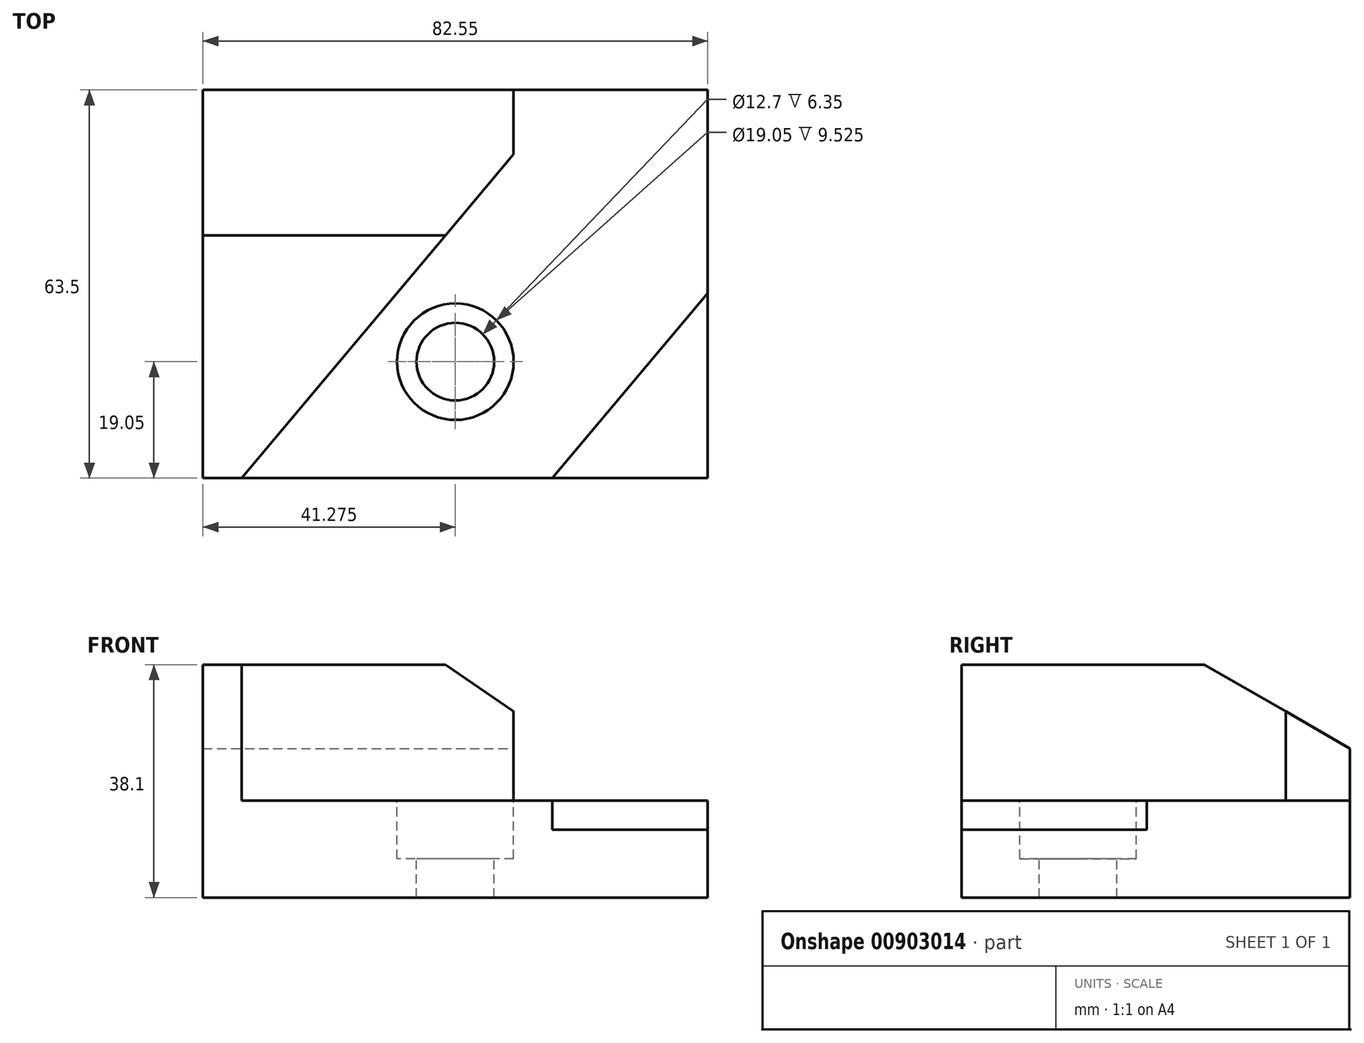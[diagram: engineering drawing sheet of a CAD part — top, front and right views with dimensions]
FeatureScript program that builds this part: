
annotation { "Feature Type Name" : "Feature", "Feature Type Description" : "" }
export const myFeature = defineFeature(function(context is Context, id is Id, definition is map)
    precondition{}
    {
        {
            var Q0;
            Q0=qCreatedBy(makeId("Front.planeOp"),FACE);
            var sketch = newSketch(context, id + "F0", { "sketchPlane" : qUnion([Q0])});
            skLineSegment(sketch, "E0.bottom", {"start": v(0, 0) * mm, "end": v(6.35, 0) * mm});
            skLineSegment(sketch, "E0.top", {"start": v(0, 38.1) * mm, "end": v(6.35, 38.1) * mm});
            skLineSegment(sketch, "E0.left", {"start": v(0, 0) * mm, "end": v(0, 38.1) * mm});
            skLineSegment(sketch, "E0.right", {"start": v(6.35, 0) * mm, "end": v(6.35, 38.1) * mm});
            skLineSegment(sketch, "E1", {"start": v(0, 0) * mm, "end": v(82.55, 0) * mm});
            skLineSegment(sketch, "E2", {"start": v(82.55, 0) * mm, "end": v(82.55, 11.11) * mm});
            skLineSegment(sketch, "E3", {"start": v(82.55, 11.11) * mm, "end": v(57.15, 11.11) * mm});
            skLineSegment(sketch, "E4", {"start": v(57.15, 11.11) * mm, "end": v(57.15, 15.87) * mm});
            skLineSegment(sketch, "E5", {"start": v(57.15, 15.87) * mm, "end": v(6.35, 15.87) * mm});
            skLineSegment(sketch, "E6", {"start": v(0, -8.47) * mm, "end": v(31.75, -8.47) * mm});
            skLineSegment(sketch, "E7.bottom", {"start": v(31.75, 0) * mm, "end": v(57.32, 0) * mm});
            skLineSegment(sketch, "E7.top", {"start": v(31.75, -4.76) * mm, "end": v(57.32, -4.76) * mm});
            skLineSegment(sketch, "E7.left", {"start": v(31.75, 0) * mm, "end": v(31.75, -4.76) * mm});
            skLineSegment(sketch, "E7.right", {"start": v(57.32, 0) * mm, "end": v(57.32, -4.76) * mm});
            skSolve(sketch);
        }
        {
            var Q0;
            {var subQ0=sQuery(id+"F0.wireOp",EDGE,"E2");Q0=makeQuery(id+"F0.imprint","IMPRINT",FACE,{"disambiguationData":[TD([[makeQuery(id+"F0.imprint","IMPRINT",EDGE,{"derivedFrom":subQ0}),1.0]])]});}
            var Q1;
            {var subQ1=sQuery(id+"F0.wireOp",EDGE,"E0.top");Q1=makeQuery(id+"F0.imprint","IMPRINT",FACE,{"disambiguationData":[TD([[makeQuery(id+"F0.imprint","IMPRINT",EDGE,{"derivedFrom":subQ1}),-1.0]])]});}
            var Q2;
            Q2=makeQuery(id+"F0.imprint","IMPRINT",FACE,{"disambiguationData":[TD([[makeQuery(id+"F0.imprint","IMPRINT",EDGE,{"derivedFrom":sQuery(id+"F0.wireOp",EDGE,"E7.bottom")}),-1.0]])]});
            extrude(context, id + "F1", {"entities" : qUnion([Q0, Q1, Q2]), "depth" : 63.5 * mm, "offsetDistance" : 25.4 * mm});
        }
        {
            var Q0;
            Q0=qCreatedBy(makeId("Top.planeOp"),FACE);
            var sketch = newSketch(context, id + "F2", { "sketchPlane" : qUnion([Q0])});
            skLineSegment(sketch, "E8", {"start": v(0, 10.1) * mm, "end": v(82.55, 10.1) * mm});
            skLineSegment(sketch, "E9", {"start": v(82.55, 0) * mm, "end": v(50.8, 0) * mm});
            skLineSegment(sketch, "E10", {"start": v(94.56, 0) * mm, "end": v(94.56, -63.5) * mm});
            skLineSegment(sketch, "E11", {"start": v(82.55, -63.5) * mm, "end": v(57.15, -63.5) * mm});
            skLineSegment(sketch, "E12", {"start": v(57.15, -63.5) * mm, "end": v(82.55, -33.23) * mm});
            skLineSegment(sketch, "E13", {"start": v(82.55, 0) * mm, "end": v(82.55, -63.5) * mm});
            skLineSegment(sketch, "E14", {"start": v(82.55, -33.23) * mm, "end": v(82.55, -63.5) * mm});
            skLineSegment(sketch, "E15", {"start": v(0, -76.09) * mm, "end": v(31.75, -76.09) * mm});
            skLineSegment(sketch, "E16", {"start": v(31.75, -76.09) * mm, "end": v(41.27, -76.09) * mm});
            skLineSegment(sketch, "E17", {"start": v(41.27, -63.5) * mm, "end": v(41.27, -44.45) * mm});
            skLineSegment(sketch, "E18", {"start": v(57.15, -63.5) * mm, "end": v(6.35, -63.5) * mm});
            skLineSegment(sketch, "E19", {"start": v(6.35, -63.5) * mm, "end": v(0, -63.5) * mm});
            skLineSegment(sketch, "E20", {"start": v(0, 0) * mm, "end": v(0, -23.81) * mm});
            skLineSegment(sketch, "E21", {"start": v(0, -23.81) * mm, "end": v(0, -63.5) * mm});
            skLineSegment(sketch, "E22", {"start": v(0, 0) * mm, "end": v(50.8, 0) * mm});
            skLineSegment(sketch, "E23", {"start": v(6.35, -63.5) * mm, "end": v(6.35, 0) * mm});
            skLineSegment(sketch, "E24", {"start": v(6.35, -63.5) * mm, "end": v(39.65, -23.81) * mm});
            skLineSegment(sketch, "E25", {"start": v(0, -23.81) * mm, "end": v(39.65, -23.81) * mm});
            skLineSegment(sketch, "E26", {"start": v(39.65, -23.81) * mm, "end": v(39.65, 0) * mm});
            skLineSegment(sketch, "E27", {"start": v(6.35, -63.5) * mm, "end": v(50.8, -10.53) * mm});
            skLineSegment(sketch, "E28", {"start": v(50.8, -10.53) * mm, "end": v(50.8, 0) * mm});
            skSolve(sketch);
        }
        {
            var Q0;
            {var subQ3=sQuery(id+"F2.wireOp",EDGE,"E9");Q0=makeQuery(id+"F2.imprint","IMPRINT",FACE,{"disambiguationData":[TD([[makeQuery(id+"F2.imprint","IMPRINT",EDGE,{"derivedFrom":subQ3}),1.0]])]});}
            extrude(context, id + "F3", {"entities" : qUnion([Q0]), "operationType" : NewBodyOperationType.ADD, "depth" : 15.88 * mm, "offsetDistance" : 25.4 * mm});
        }
        {
            var Q0;
            {var subQ3=sQuery(id+"F2.wireOp",EDGE,"E26");Q0=makeQuery(id+"F2.imprint","IMPRINT",FACE,{"disambiguationData":[TD([[makeQuery(id+"F2.imprint","IMPRINT",EDGE,{"derivedFrom":subQ3}),1.0]])]});}
            var Q1;
            {var subQ2=sQuery(id+"F2.wireOp",EDGE,"E26");Q1=makeQuery(id+"F2.imprint","IMPRINT",FACE,{"disambiguationData":[TD([[makeQuery(id+"F2.imprint","IMPRINT",EDGE,{"derivedFrom":subQ2}),-1.0]])]});}
            var Q2;
            {var subQ1=sQuery(id+"F2.wireOp",EDGE,"E23");var subQ3=sQuery(id+"F2.wireOp",EDGE,"E25");var subQ4=makeQuery(id+"F2.imprint","INTERSECT",VERTEX,{"derivedFrom":[subQ1,subQ3]});Q2=makeQuery(id+"F2.imprint","IMPRINT",FACE,{"disambiguationData":[TD([[makeQuery(id+"F2.imprint","IMPRINT",EDGE,{"disambiguationData":[TD([[subQ4,-1.0]])],"derivedFrom":subQ3}),-1.0]])]});}
            extrude(context, id + "F4", {"entities" : qUnion([Q0, Q1, Q2]), "operationType" : NewBodyOperationType.ADD, "depth" : 38.1 * mm, "offsetDistance" : 25.4 * mm});
        }
        {
            var Q0;
            Q0=makeQuery(id+"F3.boolean.opBoolean","MERGE",FACE,{"derivedFrom":[makeQuery(id+"F1.opExtrude","SWEPT_FACE",FACE,{"disambiguationData":[OSD([sQuery(id+"F0.wireOp",EDGE,"E5")])]}),makeQuery(id+"F3.opExtrude","CAP_FACE",FACE,{"disambiguationData":[OSD([sQuery(id+"F2.wireOp",EDGE,"E9"),sQuery(id+"F2.wireOp",EDGE,"E12"),sQuery(id+"F2.wireOp",EDGE,"E13"),sQuery(id+"F2.wireOp",EDGE,"E18"),sQuery(id+"F2.wireOp",EDGE,"E22"),sQuery(id+"F2.wireOp",EDGE,"E24"),sQuery(id+"F2.wireOp",EDGE,"ou16tz1h-MRkr-RfF5-7RYE-Gk9iy9VsM40f")])],"isStart":false})]});
            var sketch = newSketch(context, id + "F5", { "sketchPlane" : qUnion([Q0])});
            skLineSegment(sketch, "E29", {"start": v(0, -63.5) * mm, "end": v(31.75, -63.5) * mm});
            skPoint(sketch, "E29.startSnap0", {"position": v(31.75, -63.5) * mm});
            skLineSegment(sketch, "E30", {"start": v(31.75, -63.5) * mm, "end": v(41.28, -63.5) * mm});
            skLineSegment(sketch, "E31", {"start": v(41.28, -63.5) * mm, "end": v(41.28, -44.45) * mm});
            skSolve(sketch);
        }
        {
            var Q0;
            Q0=sQuery(id+"F5.wireOp",VERTEX,"E31.end");
            var Q1;
            Q1=makeQuery(id+"F1.opExtrude","SWEPT_BODY",BODY,{"disambiguationData":[OSD([sQuery(id+"F0.wireOp",EDGE,"E0.top"),sQuery(id+"F0.wireOp",EDGE,"E0.left"),sQuery(id+"F0.wireOp",EDGE,"E0.right"),sQuery(id+"F0.wireOp",EDGE,"E1"),sQuery(id+"F0.wireOp",EDGE,"E2"),sQuery(id+"F0.wireOp",EDGE,"E3"),sQuery(id+"F0.wireOp",EDGE,"E4"),sQuery(id+"F0.wireOp",EDGE,"E5"),sQuery(id+"F0.wireOp",EDGE,"E7.top"),sQuery(id+"F0.wireOp",EDGE,"E7.left"),sQuery(id+"F0.wireOp",EDGE,"E7.right")])]});
            hole(context, id + "F6", {"style" : HoleStyle.C_BORE, "endStyle" : HoleEndStyle.THROUGH, "holeDiameter" : 12.7 * mm, "cBoreDiameter" : 19.05 * mm, "cBoreDepth" : 9.52 * mm, "majorDiameter" : 6.35 * mm, "isTappedThrough" : true, "tappedDepth" : 12.7 * mm, "tapClearance" : 3, "locations" : qUnion([Q0]), "scope" : qUnion([Q1])});
        }
        {
            var Q0;
            Q0=makeQuery(id+"F4.opExtrude","SWEPT_FACE",FACE,{"disambiguationData":[OSD([sQuery(id+"F2.wireOp",EDGE,"E28")])]});
            var sketch = newSketch(context, id + "F7", { "sketchPlane" : qUnion([Q0])});
            skLineSegment(sketch, "E32", {"start": v(0, 38.1) * mm, "end": v(-23.81, 38.1) * mm});
            skLineSegment(sketch, "E33", {"start": v(-23.81, 38.1) * mm, "end": v(0, 24.35) * mm});
            skSolve(sketch);
        }
        {
            var Q0;
            {var subQ0=sQuery(id+"F7.wireOp",EDGE,"E32");var subQ3=sQuery(id+"F7.wireOp",EDGE,"E33");var subQ4=makeQuery(id+"F7.imprint","INTERSECT",VERTEX,{"derivedFrom":[subQ0,subQ3]});Q0=makeQuery(id+"F7.imprint","IMPRINT",FACE,{"disambiguationData":[TD([[makeQuery(id+"F7.imprint","IMPRINT",EDGE,{"disambiguationData":[TD([[subQ4,1.0]])],"derivedFrom":subQ0}),1.0]])]});}
            var Q1;
            {var subQ0=sQuery(id+"F7.wireOp",EDGE,"E32");var subQ1=sQuery(id+"F2.wireOp",EDGE,"E28");var subQ2=makeQuery(id+"F4.opExtrude","SWEPT_EDGE",EDGE,{"disambiguationData":[OSD([sQuery(id+"F2.wireOp",EDGE,"E9"),sQuery(id+"F2.wireOp",EDGE,"E22"),subQ1])]});var subQ3=makeQuery(id+"F7.imprint","INTERSECT",VERTEX,{"derivedFrom":[subQ2,subQ0]});Q1=makeQuery(id+"F7.imprint","IMPRINT",FACE,{"disambiguationData":[TD([[makeQuery(id+"F7.imprint","IMPRINT",EDGE,{"disambiguationData":[TD([[subQ3,1.0]])],"derivedFrom":subQ0}),-1.0]])]});}
            extrude(context, id + "F8", {"entities" : qUnion([Q0, Q1]), "operationType" : NewBodyOperationType.REMOVE, "oppositeDirection" : true, "depth" : 50.8 * mm, "offsetDistance" : 25.4 * mm});
        }
    });
